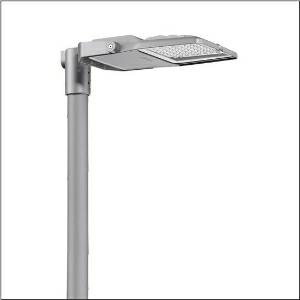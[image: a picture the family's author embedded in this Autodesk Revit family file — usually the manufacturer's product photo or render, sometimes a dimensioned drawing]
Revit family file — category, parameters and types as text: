
# Revit family: floodlight_fl_21_iq_mini___pl64_5xa7772d2e3a_5308
name_source: partatom
category: Lighting Fixtures
units: mm (PartAtom-declared; Revit-internal decimal feet)

## family parameters
Cut with Voids When Loaded = No
Host = Face
Light Source = No
Part Type = Normal
Room Calculation Point = No
Round Connector Dimension = Use Diameter
Shared = No

## types (1)
- --- (1 x LED, 17220 lm, 143 W, 3000K)
    Apparent Load = 143 VA
    CIE Flux Codes = 28 80 98 100 100
    Color Rendering = 70
    Color Temperature = 3000K
    Default Elevation = 1800 mm
    Description = Floodlight FL 21 iQ mini, floodlight, primary light control with lens, of PMMA, primary optical cover: protective disc, of toughened safety glass, transparent, light distribution: PL64, light emission: direct distribution, installation type: surface-mounted, LED, High Power LED, rated luminous flux: 17.220lm, luminous efficacy: 120lm/W, light colour: 730, colour temperature: 3000K, control gear: iQ Street-Remote/DALI, control: Auto-Match, Temp-Guard, Night-Set, Smart-Wire, Desk-Remote (wireless, voltage-free reading and setting of iQ features in the workshop via application-optimized NFC function/RFID function), optimised constant luminous flux control (CLO 2.0), Light-Fading, Lumen-Switch, with terminal, 6-pole, mains connection: 220..240V, AC, 50/60Hz, start of lifetime: 143W, end of service life: 152W, reduction: 61W, luminaire housing, of diecast aluminium, powder-coated, Siteco® metallic grey (DB 702S), corrosivity category C5 mid according to DIN EN ISO 12944, suitable for swimming pools, chlorine-resistant, sealing non-destructively replaceable, please order mast flange separately, mast bracket, of steel, galvanised, powder-coated, protection rating (complete): IP66, insulation class (complete): insulation class II (safety insulation), certification: CE, ENEC, VDE, protection symbol: D, impact resistance: IK08, permissible operating ambient temperature: -40..+40°C, permissible operating ambient temperature for outdoor applications: -40..+50°C, standard: DIN EN 12944, LABS conformity tested according to VDMA 24364:2018-05, packaging unit: 1 piece

Light Distribution: PL64
    Height = 70 mm
    Lamp = 1 x LED
    Lamp Light Flux = 17220 lm
    Lamp Power = 143 W
    Lamp count = 1
    Length = 485 mm
    Luminous efficacy = 120 lm/W
    Manufacturer = Siteco
    ModVariant = No
    Model = 5XA7772D2E3A
    Number of Poles = 1
    OnlyDefault = Yes
    Power Factor = 1
    Product Name = Floodlight FL 21 iQ mini | PL64
    Product group = floodlight | pylon annexe
    ProductGroupID = 6200
    Protection Class = Protection class II
    Protection Degree = IP 66
    RLX_Detail_Level = 1
    RLX_Emergency_Light_Flux = 0 lm
    RLX_Emergency_Type = 0
    RLX_Emergency_Type_DB = No
    RlxData = <blob elided: 101629 chars, md5=e41ba6a2>
    Socket = socket
    Standby Power = 0 W
    System Light Flux = 17220 lm
    System Power = 143 W
    Type Comments = factory setting: luminous flux: 100 % | dim-lin: 254 | 730 mA
    Type Image = l_1007125.jpg
    URL = http://relux.com
    VarID = @adj_165802
    Voltage = 0 V
    Weight = 0.00 kg
    Width = 337 mm

## geometry (parser evidence)
native form markers: Blend x4, Sweep x14
no freeform markers — native parametric forms only
